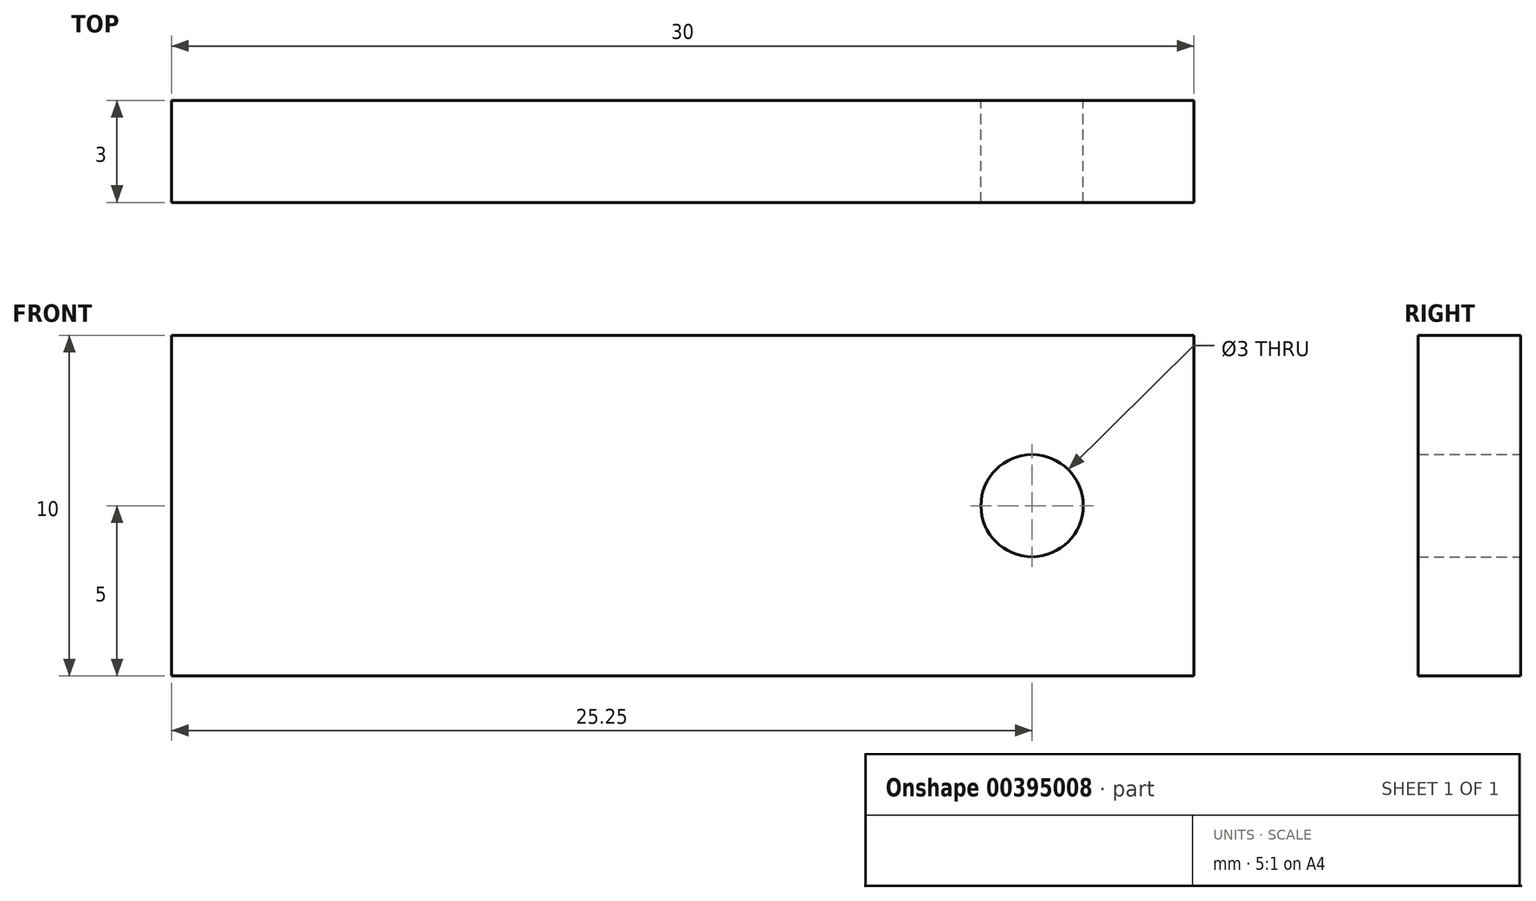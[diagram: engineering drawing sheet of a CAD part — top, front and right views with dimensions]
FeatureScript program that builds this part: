
annotation { "Feature Type Name" : "Feature", "Feature Type Description" : "" }
export const myFeature = defineFeature(function(context is Context, id is Id, definition is map)
    precondition{}
    {
        {
            var Q0;
            Q0=qCreatedBy(makeId("Top.planeOp"),FACE);
            var sketch = newSketch(context, id + "F0", { "sketchPlane" : qUnion([Q0])});
            skCircle(sketch, "E0", {"center": v(0, 0) * mm, "radius": 13.75 * mm});
            skCircle(sketch, "E1.0", {"center": v(0, 0) * mm, "radius": 16.75 * mm});
            skLineSegment(sketch, "E2.bottom", {"start": v(-25, -4) * mm, "end": v(25, -4) * mm});
            skLineSegment(sketch, "E2.top", {"start": v(-25, 4) * mm, "end": v(25, 4) * mm});
            skLineSegment(sketch, "E2.left", {"start": v(-25, -4) * mm, "end": v(-25, 4) * mm});
            skLineSegment(sketch, "E2.right", {"start": v(25, -4) * mm, "end": v(25, 4) * mm});
            skLineSegment(sketch, "E3.bottom", {"start": v(-25, -1) * mm, "end": v(25, -1) * mm});
            skLineSegment(sketch, "E3.top", {"start": v(-25, 1) * mm, "end": v(25, 1) * mm});
            skLineSegment(sketch, "E3.left", {"start": v(-25, -1) * mm, "end": v(-25, 1) * mm});
            skLineSegment(sketch, "E3.right", {"start": v(25, -1) * mm, "end": v(25, 1) * mm});
            skLineSegment(sketch, "E4.bottom", {"start": v(-4.5, -23.5) * mm, "end": v(4.5, -23.5) * mm});
            skLineSegment(sketch, "E4.top", {"start": v(-4.5, 23.5) * mm, "end": v(4.5, 23.5) * mm});
            skLineSegment(sketch, "E4.left", {"start": v(-4.5, -23.5) * mm, "end": v(-4.5, 23.5) * mm});
            skLineSegment(sketch, "E4.right", {"start": v(4.5, -23.5) * mm, "end": v(4.5, 23.5) * mm});
            skLineSegment(sketch, "E5.bottom", {"start": v(15, 22) * mm, "end": v(-15, 22) * mm});
            skLineSegment(sketch, "E5.top", {"start": v(15, 25) * mm, "end": v(-15, 25) * mm});
            skLineSegment(sketch, "E5.left", {"start": v(15, 22) * mm, "end": v(15, 25) * mm});
            skLineSegment(sketch, "E5.right", {"start": v(-15, 22) * mm, "end": v(-15, 25) * mm});
            skPoint(sketch, "E5.middle", {"position": v(0, 23.5) * mm});
            skSolve(sketch);
        }
        {
            var Q0;
            {var subQ5=sQuery(id+"F0.wireOp",EDGE,"E4.top");Q0=makeQuery(id+"F0.imprint","IMPRINT",FACE,{"disambiguationData":[TD([[makeQuery(id+"F0.imprint","IMPRINT",EDGE,{"derivedFrom":subQ5}),1.0]])]});}
            var Q1;
            {var subQ0=sQuery(id+"F0.wireOp",EDGE,"E4.top");Q1=makeQuery(id+"F0.imprint","IMPRINT",FACE,{"disambiguationData":[TD([[makeQuery(id+"F0.imprint","IMPRINT",EDGE,{"derivedFrom":subQ0}),-1.0]])]});}
            extrude(context, id + "F1", {"entities" : qUnion([Q0, Q1]), "depth" : 10 * mm});
        }
        {
            var Q0;
            Q0=makeQuery(id+"F1.opExtrude","SWEPT_FACE",FACE,{"disambiguationData":[OSD([sQuery(id+"F0.wireOp",EDGE,"E5.top")])]});
            cPlane(context, id + "F2", {"entities" : qUnion([Q0]), "cplaneType" : CPlaneType.OFFSET, "offset" : 0 * mm, "width" : 150 * mm, "height" : 150 * mm});
        }
        {
            var Q0;
            Q0=qCreatedBy(id+"F2.planeOp",FACE);
            var sketch = newSketch(context, id + "F3", { "sketchPlane" : qUnion([Q0])});
            skLineSegment(sketch, "E6", {"start": v(0, 0) * mm, "end": v(0, 5) * mm, "construction": true});
            skLineSegment(sketch, "E7", {"start": v(0, 5) * mm, "end": v(-10.25, 5) * mm, "construction": true});
            skCircle(sketch, "E8", {"center": v(-10.25, 5) * mm, "radius": 1.5 * mm});
            skCircle(sketch, "E9.MirrorC", {"center": v(10.25, 5) * mm, "radius": 1.5 * mm});
            skLineSegment(sketch, "E10", {"start": v(-10.25, 5) * mm, "end": v(-22.25, 5) * mm, "construction": true});
            skCircle(sketch, "E11", {"center": v(-22.25, 5) * mm, "radius": 1.5 * mm});
            skSolve(sketch);
        }
        {
            var Q0;
            Q0=makeQuery(id+"F3.imprint","IMPRINT",FACE,{"disambiguationData":[TD([[makeQuery(id+"F3.imprint","IMPRINT",EDGE,{"derivedFrom":sQuery(id+"F3.wireOp",EDGE,"E9.MirrorC")}),-1.0]])]});
            var Q1;
            Q1=makeQuery(id+"F3.imprint","IMPRINT",FACE,{"disambiguationData":[TD([[makeQuery(id+"F3.imprint","IMPRINT",EDGE,{"derivedFrom":sQuery(id+"F3.wireOp",EDGE,"E8")}),1.0]])]});
            extrude(context, id + "F4", {"entities" : qUnion([Q0, Q1]), "operationType" : NewBodyOperationType.REMOVE, "endBound" : BoundingType.UP_TO_NEXT, "oppositeDirection" : true, "depth" : 25 * mm});
        }
        {
            var Q0;
            Q0=makeQuery(id+"F3.imprint","IMPRINT",FACE,{"disambiguationData":[TD([[makeQuery(id+"F3.imprint","IMPRINT",EDGE,{"derivedFrom":sQuery(id+"F3.wireOp",EDGE,"E11")}),1.0]])]});
            extrude(context, id + "F5", {"entities" : qUnion([Q0]), "operationType" : NewBodyOperationType.REMOVE, "endBound" : BoundingType.THROUGH_ALL, "oppositeDirection" : true, "depth" : 25 * mm});
        }
    });
